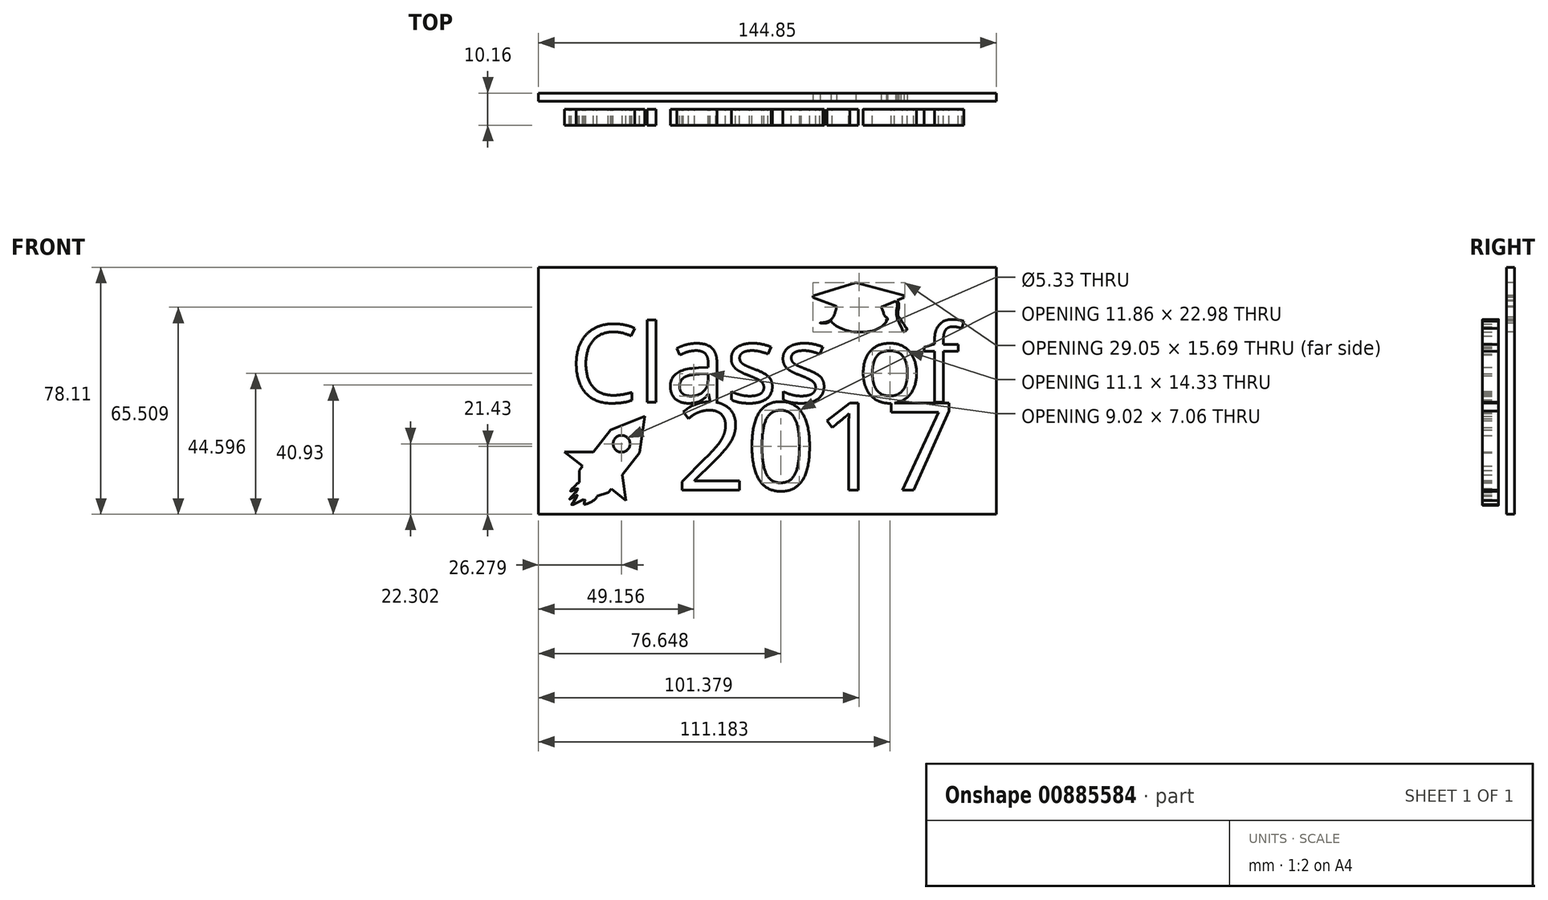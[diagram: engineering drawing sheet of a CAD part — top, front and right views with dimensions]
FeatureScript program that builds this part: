
annotation { "Feature Type Name" : "Feature", "Feature Type Description" : "" }
export const myFeature = defineFeature(function(context is Context, id is Id, definition is map)
    precondition{}
    {
        {
            var Q0;
            Q0=qCreatedBy(makeId("Front.planeOp"),FACE);
            var sketch = newSketch(context, id + "F0", { "sketchPlane" : qUnion([Q0])});
            skLineSegment(sketch, "E0.bottom", {"start": v(-72.33, 44.27) * mm, "end": v(72.52, 44.27) * mm});
            skLineSegment(sketch, "E0.top", {"start": v(-72.33, -33.84) * mm, "end": v(72.52, -33.84) * mm});
            skLineSegment(sketch, "E0.left", {"start": v(-72.33, 44.27) * mm, "end": v(-72.33, -33.84) * mm});
            skLineSegment(sketch, "E0.right", {"start": v(72.52, 44.27) * mm, "end": v(72.52, -33.84) * mm});
            skSolve(sketch);
        }
        {
            var Q0;
            Q0=makeQuery(id+"F0.imprint","IMPRINT",FACE,{"disambiguationData":[TD([[makeQuery(id+"F0.imprint","IMPRINT",EDGE,{"derivedFrom":sQuery(id+"F0.wireOp",EDGE,"E0.bottom")}),-1.0]])]});
            extrude(context, id + "F1", {"entities" : qUnion([Q0]), "depth" : 2.54 * mm, "offsetDistance" : 25.4 * mm});
        }
        {
            var Q0;
            Q0=qCreatedBy(makeId("Front.planeOp"),FACE);
            cPlane(context, id + "F2", {"entities" : qUnion([Q0]), "cplaneType" : CPlaneType.OFFSET, "offset" : 5.08 * mm, "width" : 152.4 * mm, "height" : 152.4 * mm});
        }
        {
            var Q0;
            Q0=qCreatedBy(id+"F2.planeOp",FACE);
            var sketch = newSketch(context, id + "F3", { "sketchPlane" : qUnion([Q0])});
            skText(sketch, "E1", { "text": "Class of", "fontName": "OpenSans-Regular.ttf"});
            skText(sketch, "E2", { "text": "2017", "fontName": "OpenSans-Regular.ttf"});
            const initialGuessF3  = {"E1": [-0.06247, 0.0016, 1, 0, 0.02468], "E2": [-0.0288, -0.02622, 1, 0, 0.02782]};
            skSetInitialGuess(sketch, initialGuessF3);
            skSolve(sketch);
        }
        {
            var Q0;
            Q0 = qSketchRegion(id + "F3", true);
            extrude(context, id + "F4", {"entities" : qUnion([Q0]), "operationType" : NewBodyOperationType.ADD, "depth" : 5.08 * mm, "offsetDistance" : 25.4 * mm});
        }
        {
            var Q0;
            Q0=qCreatedBy(id+"F2.planeOp",FACE);
            var sketch = newSketch(context, id + "F5", { "sketchPlane" : qUnion([Q0])});
            skLineSegment(sketch, "E3", {"start": v(-38.7, -2.82) * mm, "end": v(-49.54, -7.2) * mm});
            skLineSegment(sketch, "E4", {"start": v(-40.33, -14.4) * mm, "end": v(-38.7, -2.82) * mm});
            skLineSegment(sketch, "E5", {"start": v(-49.54, -7.2) * mm, "end": v(-59.4, -19.92) * mm});
            skLineSegment(sketch, "E6", {"start": v(-59.4, -19.92) * mm, "end": v(-50.23, -27.02) * mm});
            skLineSegment(sketch, "E7", {"start": v(-50.23, -27.02) * mm, "end": v(-40.33, -14.4) * mm});
            skLineSegment(sketch, "E8", {"start": v(-54.93, -14.17) * mm, "end": v(-64.13, -14.17) * mm});
            skLineSegment(sketch, "E9", {"start": v(-64.13, -14.17) * mm, "end": v(-58.38, -18.62) * mm});
            skLineSegment(sketch, "E10", {"start": v(-45.78, -21.34) * mm, "end": v(-44.62, -29.52) * mm});
            skLineSegment(sketch, "E11", {"start": v(-44.62, -29.52) * mm, "end": v(-49.3, -25.82) * mm});
            skLineSegment(sketch, "E12", {"start": v(-59.4, -19.92) * mm, "end": v(-59.4, -23.82) * mm});
            skLineSegment(sketch, "E13", {"start": v(-59.4, -23.82) * mm, "end": v(-53.82, -28.13) * mm});
            skLineSegment(sketch, "E14", {"start": v(-53.82, -28.13) * mm, "end": v(-50.23, -27.02) * mm});
            skCircle(sketch, "E15", {"center": v(-46.05, -11.54) * mm, "radius": 2.67 * mm});
            skLineSegment(sketch, "E16", {"start": v(-79.47, -28.09) * mm, "end": v(-79.47, -28.09) * mm});
            skLineSegment(sketch, "E17", {"start": v(-57.93, -30.77) * mm, "end": v(-53.82, -28.13) * mm});
            skFitSpline(sketch, "E18", {"points": [v(-59.4, -23.82) * mm, v(-60.45, -24.56) * mm, v(-61.42, -25.46) * mm, v(-62.18, -26.65) * mm, v(-59.86, -25.72) * mm, v(-62.55, -29.05) * mm, v(-62.18, -28.95) * mm, v(-59.99, -27.85) * mm, v(-61.92, -30.95) * mm, v(-57.73, -29.14) * mm, v(-57.98, -30.67) * mm, v(-57.93, -30.77) * mm, v(-53.82, -28.13) * mm, v(-59.4, -23.82) * mm]});
            skSolve(sketch);
        }
        {
            var Q0;
            Q0 = qSketchRegion(id + "F5", true);
            extrude(context, id + "F6", {"entities" : qUnion([Q0]), "depth" : 5.08 * mm, "offsetDistance" : 25.4 * mm});
        }
        {
            var Q0;
            Q0=qCreatedBy(id+"F2.planeOp",FACE);
            var sketch = newSketch(context, id + "F7", { "sketchPlane" : qUnion([Q0])});
            skFitSpline(sketch, "E19.trimOffspring", {"points": [v(22, 32.05) * mm, v(20.23, 27.8) * mm, v(16.76, 26.72) * mm, v(20.23, 27.37) * mm, v(22, 32.05) * mm]});
            skPoint(sketch, "E20.orphan", {"position": v(22, 32.13) * mm});
            skLineSegment(sketch, "E21", {"start": v(20.23, 27.8) * mm, "end": v(20.23, 27.37) * mm});
            skLineSegment(sketch, "E22", {"start": v(21.98, 31.98) * mm, "end": v(14.52, 34.77) * mm});
            skLineSegment(sketch, "E23", {"start": v(14.52, 34.77) * mm, "end": v(14.52, 35.25) * mm});
            skLineSegment(sketch, "E24", {"start": v(14.52, 35.25) * mm, "end": v(28.11, 39.51) * mm});
            skLineSegment(sketch, "E25", {"start": v(28.11, 39.51) * mm, "end": v(43.35, 35.35) * mm});
            skLineSegment(sketch, "E26", {"start": v(43.35, 35.35) * mm, "end": v(43.35, 34.7) * mm});
            skLineSegment(sketch, "E27", {"start": v(43.35, 34.7) * mm, "end": v(36.03, 31.73) * mm});
            skFitSpline(sketch, "E28.trimOffspring", {"points": [v(36.03, 31.73) * mm, v(36.51, 29.46) * mm, v(37.8, 27.84) * mm, v(38.13, 27.66) * mm, v(38.1, 28.05) * mm, v(37.24, 28.92) * mm, v(36.77, 30.19) * mm, v(36.03, 31.73) * mm]});
            skPoint(sketch, "E29.orphan", {"position": v(37.8, 27.32) * mm});
            skLineSegment(sketch, "E30", {"start": v(37.8, 27.84) * mm, "end": v(37.8, 27.32) * mm});
            skFitSpline(sketch, "E31", {"points": [v(37.8, 27.32) * mm, v(36.25, 25.6) * mm, v(33.4, 24.26) * mm, v(30.04, 23.85) * mm, v(26.67, 23.95) * mm, v(22.63, 25.37) * mm, v(20.23, 27.37) * mm, v(20.96, 27.8) * mm, v(30.2, 26.9) * mm, v(36.73, 27.56) * mm, v(37.8, 27.32) * mm]});
            skFitSpline(sketch, "E32", {"points": [v(40.7, 33.62) * mm, v(41.01, 33.19) * mm, v(41.2, 32.3) * mm, v(40.97, 30.76) * mm, v(40.9, 29.36) * mm, v(41.22, 28.2) * mm, v(41.13, 27.85) * mm, v(41.28, 27.37) * mm, v(41.69, 27.08) * mm, v(41.84, 26.52) * mm, v(42.55, 25.2) * mm, v(42.85, 24.62) * mm, v(42.94, 23.91) * mm, v(43.44, 23.96) * mm, v(44.33, 24.53) * mm, v(44.36, 24.8) * mm, v(43.89, 25.26) * mm, v(43.26, 26.34) * mm, v(42.96, 26.8) * mm, v(42.32, 27.5) * mm, v(42.3, 27.97) * mm, v(41.73, 28.5) * mm, v(41.55, 28.5) * mm, v(41.4, 29.72) * mm, v(41.61, 31.33) * mm, v(41.67, 32.89) * mm, v(41.2, 33.82) * mm, v(40.7, 33.62) * mm]});
            skSolve(sketch);
        }
        {
            var Q0;
            Q0 = qSketchRegion(id + "F7", true);
            extrude(context, id + "F8", {"entities" : qUnion([Q0]), "operationType" : NewBodyOperationType.REMOVE, "oppositeDirection" : true, "depth" : 25.4 * mm, "offsetDistance" : 25.4 * mm});
        }
    });
